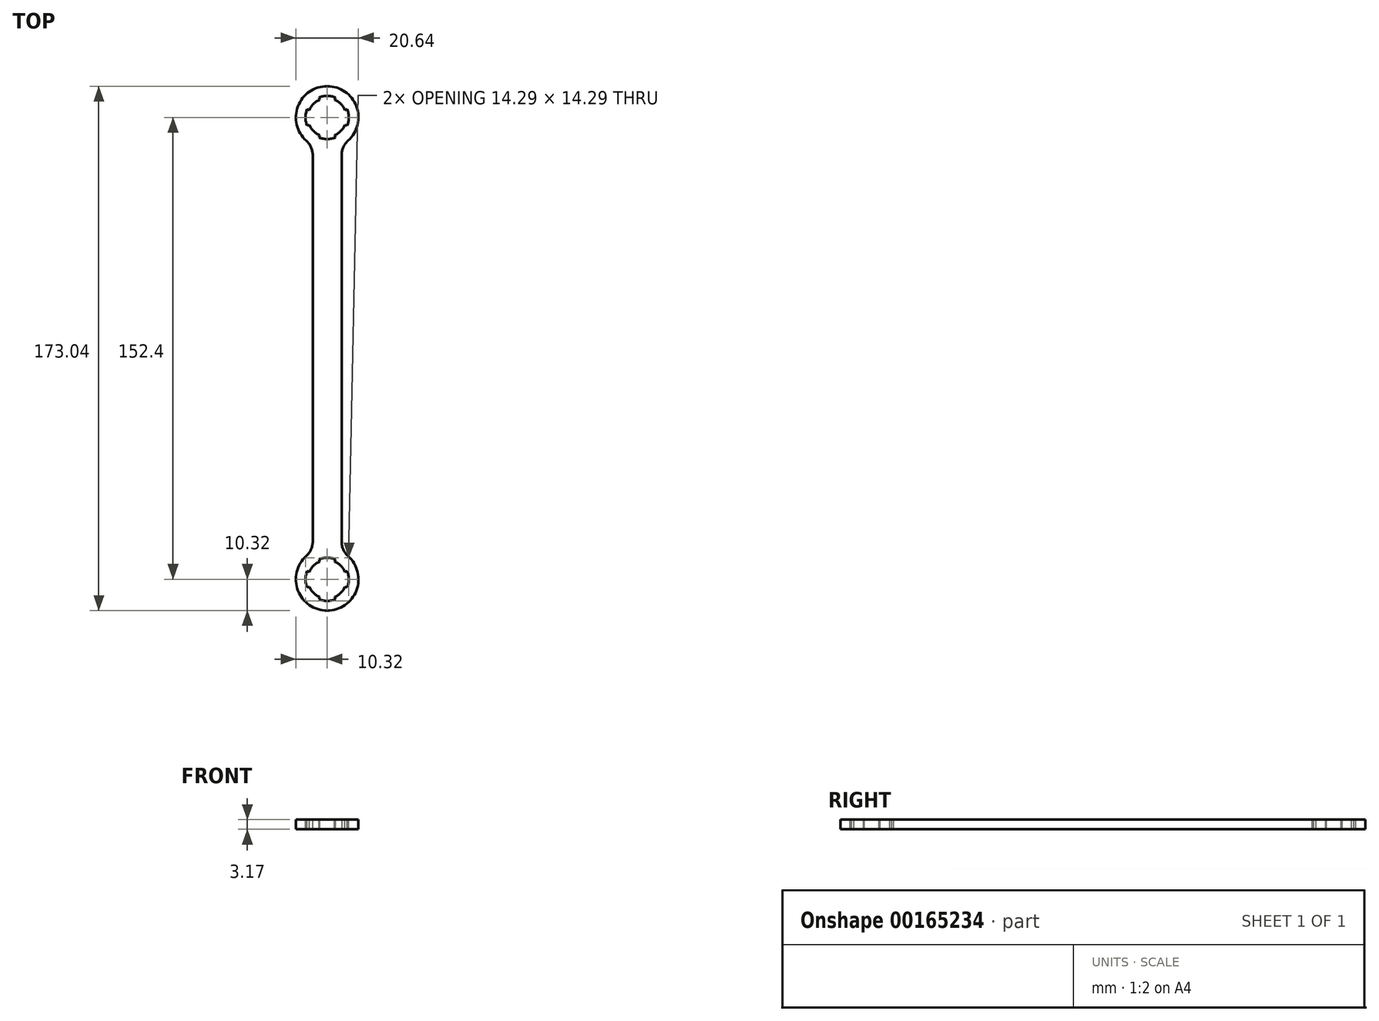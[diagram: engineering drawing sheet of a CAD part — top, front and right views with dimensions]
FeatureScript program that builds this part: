
annotation { "Feature Type Name" : "Feature", "Feature Type Description" : "" }
export const myFeature = defineFeature(function(context is Context, id is Id, definition is map)
    precondition{}
    {
        {
            var Q0;
            Q0=qCreatedBy(makeId("Top.planeOp"),FACE);
            var sketch = newSketch(context, id + "F0", { "sketchPlane" : qUnion([Q0])});
            skArc(sketch, "E0", {"start": v(4.76, -9.15) * mm, "mid": v(0, 10.32) * mm, "end": v(-4.76, -9.15) * mm});
            skCircle(sketch, "E1", {"center": v(0, 0) * mm, "radius": 6.35 * mm});
            skLineSegment(sketch, "E2", {"start": v(0, 0) * mm, "end": v(0, -152.4) * mm, "construction": true});
            skCircle(sketch, "E3", {"center": v(0, -152.4) * mm, "radius": 6.35 * mm});
            skLineSegment(sketch, "E4.bottom", {"start": v(4.76, -9.15) * mm, "end": v(-4.76, -9.15) * mm, "construction": true});
            skLineSegment(sketch, "E4.top", {"start": v(4.76, -143.25) * mm, "end": v(-4.76, -143.25) * mm, "construction": true});
            skLineSegment(sketch, "E4.left", {"start": v(4.76, -9.15) * mm, "end": v(4.76, -143.25) * mm});
            skLineSegment(sketch, "E4.right", {"start": v(-4.76, -9.15) * mm, "end": v(-4.76, -143.25) * mm});
            skPoint(sketch, "E4.middle", {"position": v(0, -76.2) * mm});
            skArc(sketch, "E5", {"start": v(-4.76, -143.25) * mm, "mid": v(0, -162.72) * mm, "end": v(4.76, -143.25) * mm});
            skSolve(sketch);
        }
        {
            var Q0;
            Q0 = qSketchRegion(id + "F0", true);
            extrude(context, id + "F1", {"entities" : qUnion([Q0]), "depth" : 3.17 * mm});
        }
        {
            var Q0;
            Q0=makeQuery(id+"F1.opExtrude","SWEPT_EDGE",EDGE,{"disambiguationData":[OSD([sQuery(id+"F0.wireOp",EDGE,"E0"),sQuery(id+"F0.wireOp",EDGE,"E4.left")])]});
            var Q1;
            Q1=makeQuery(id+"F1.opExtrude","SWEPT_EDGE",EDGE,{"disambiguationData":[OSD([sQuery(id+"F0.wireOp",EDGE,"E0"),sQuery(id+"F0.wireOp",EDGE,"E4.right")])]});
            var Q2;
            Q2=makeQuery(id+"F1.opExtrude","SWEPT_EDGE",EDGE,{"disambiguationData":[OSD([sQuery(id+"F0.wireOp",EDGE,"E4.right"),sQuery(id+"F0.wireOp",EDGE,"E5")])]});
            var Q3;
            Q3=makeQuery(id+"F1.opExtrude","SWEPT_EDGE",EDGE,{"disambiguationData":[OSD([sQuery(id+"F0.wireOp",EDGE,"E4.left"),sQuery(id+"F0.wireOp",EDGE,"E5")])]});
            fillet(context, id + "F2", {"entities" : qUnion([Q0, Q1, Q2, Q3]), "radius" : 6.35 * mm, "tangentPropagation" : true, "allowEdgeOverflow" : false});
        }
        {
            var Q0;
            Q0=makeQuery(id+"F1.opExtrude","CAP_FACE",FACE,{"disambiguationData":[OSD([sQuery(id+"F0.wireOp",EDGE,"E0"),sQuery(id+"F0.wireOp",EDGE,"E1"),sQuery(id+"F0.wireOp",EDGE,"E3"),sQuery(id+"F0.wireOp",EDGE,"E4.left"),sQuery(id+"F0.wireOp",EDGE,"E4.right"),sQuery(id+"F0.wireOp",EDGE,"E5")])],"isStart":false});
            var sketch = newSketch(context, id + "F3", { "sketchPlane" : qUnion([Q0])});
            skLineSegment(sketch, "E6", {"start": v(0, -152.4) * mm, "end": v(-6.35, -152.4) * mm, "construction": true});
            skLineSegment(sketch, "E7", {"start": v(0, -152.4) * mm, "end": v(-5.87, -154.83) * mm, "construction": true});
            skLineSegment(sketch, "E8", {"start": v(0, -152.4) * mm, "end": v(-5.87, -149.97) * mm, "construction": true});
            skArc(sketch, "E9", {"start": v(-5.87, -149.97) * mm, "mid": v(-6.35, -152.4) * mm, "end": v(-5.87, -154.83) * mm});
            skLineSegment(sketch, "E10", {"start": v(-5.87, -154.83) * mm, "end": v(-6.6, -155.13) * mm});
            skLineSegment(sketch, "E11", {"start": v(-5.87, -149.97) * mm, "end": v(-6.6, -149.67) * mm});
            skArc(sketch, "E12", {"start": v(-6.6, -149.67) * mm, "mid": v(-7.14, -152.4) * mm, "end": v(-6.6, -155.13) * mm});
            skLineSegment(sketch, "E13", {"start": v(0, 0) * mm, "end": v(-6.35, 0) * mm, "construction": true});
            skLineSegment(sketch, "E14", {"start": v(0, 0) * mm, "end": v(-5.87, 2.43) * mm, "construction": true});
            skLineSegment(sketch, "E15", {"start": v(0, 0) * mm, "end": v(-5.87, -2.43) * mm, "construction": true});
            skArc(sketch, "E16", {"start": v(-5.87, 2.43) * mm, "mid": v(-6.35, 0) * mm, "end": v(-5.87, -2.43) * mm});
            skLineSegment(sketch, "E17", {"start": v(-5.87, -2.43) * mm, "end": v(-6.6, -2.73) * mm});
            skLineSegment(sketch, "E18", {"start": v(-5.87, 2.43) * mm, "end": v(-6.6, 2.73) * mm});
            skArc(sketch, "E19", {"start": v(-6.6, 2.73) * mm, "mid": v(-7.14, 0) * mm, "end": v(-6.6, -2.73) * mm});
            skSolve(sketch);
        }
        {
            var Q0;
            Q0 = qSketchRegion(id + "F3", true);
            var Q1;
            Q1=makeQuery(id+"F1.opExtrude","CAP_FACE",FACE,{"disambiguationData":[OSD([sQuery(id+"F0.wireOp",EDGE,"E0"),sQuery(id+"F0.wireOp",EDGE,"E1"),sQuery(id+"F0.wireOp",EDGE,"E3"),sQuery(id+"F0.wireOp",EDGE,"E4.left"),sQuery(id+"F0.wireOp",EDGE,"E4.right"),sQuery(id+"F0.wireOp",EDGE,"E5")])],"isStart":true});
            extrude(context, id + "F4", {"entities" : qUnion([Q0]), "operationType" : NewBodyOperationType.REMOVE, "endBound" : BoundingType.UP_TO_SURFACE, "oppositeDirection" : true, "endBoundEntityFace" : qUnion([Q1]), "depth" : 25.4 * mm});
        }
        {
            var Q0;
            Q0=makeQuery(id+"F4.boolean.opBoolean","COPY",FACE,{"derivedFrom":makeQuery(id+"F4.opExtrude","SWEPT_FACE",FACE,{"disambiguationData":[OSD([sQuery(id+"F3.wireOp",EDGE,"E10")])]})});
            var Q1;
            Q1=makeQuery(id+"F4.boolean.opBoolean","COPY",FACE,{"derivedFrom":makeQuery(id+"F4.opExtrude","SWEPT_FACE",FACE,{"disambiguationData":[OSD([sQuery(id+"F3.wireOp",EDGE,"E12")])]})});
            var Q2;
            Q2=makeQuery(id+"F4.boolean.opBoolean","COPY",FACE,{"derivedFrom":makeQuery(id+"F4.opExtrude","SWEPT_FACE",FACE,{"disambiguationData":[OSD([sQuery(id+"F3.wireOp",EDGE,"E11")])]})});
            var Q3;
            Q3=makeQuery(id+"F1.opExtrude","SWEPT_FACE",FACE,{"disambiguationData":[OSD([sQuery(id+"F0.wireOp",EDGE,"E3")])]});
            circularPattern(context, id + "F5", {"patternType" : PatternType.FACE, "faces" : qUnion([Q0, Q1, Q2]), "axis" : qUnion([Q3]), "angle" : 360 * degree, "instanceCount" : 4, "equalSpace" : true});
        }
        {
            var Q0;
            Q0=makeQuery(id+"F4.boolean.opBoolean","COPY",FACE,{"derivedFrom":makeQuery(id+"F4.opExtrude","SWEPT_FACE",FACE,{"disambiguationData":[OSD([sQuery(id+"F3.wireOp",EDGE,"E18")])]})});
            var Q1;
            Q1=makeQuery(id+"F4.boolean.opBoolean","COPY",FACE,{"derivedFrom":makeQuery(id+"F4.opExtrude","SWEPT_FACE",FACE,{"disambiguationData":[OSD([sQuery(id+"F3.wireOp",EDGE,"E19")])]})});
            var Q2;
            Q2=makeQuery(id+"F4.boolean.opBoolean","COPY",FACE,{"derivedFrom":makeQuery(id+"F4.opExtrude","SWEPT_FACE",FACE,{"disambiguationData":[OSD([sQuery(id+"F3.wireOp",EDGE,"E17")])]})});
            var Q3;
            Q3=makeQuery(id+"F1.opExtrude","SWEPT_FACE",FACE,{"disambiguationData":[OSD([sQuery(id+"F0.wireOp",EDGE,"E1")])]});
            circularPattern(context, id + "F6", {"patternType" : PatternType.FACE, "faces" : qUnion([Q0, Q1, Q2]), "axis" : qUnion([Q3]), "angle" : 360 * degree, "instanceCount" : 4, "equalSpace" : true});
        }
    });
